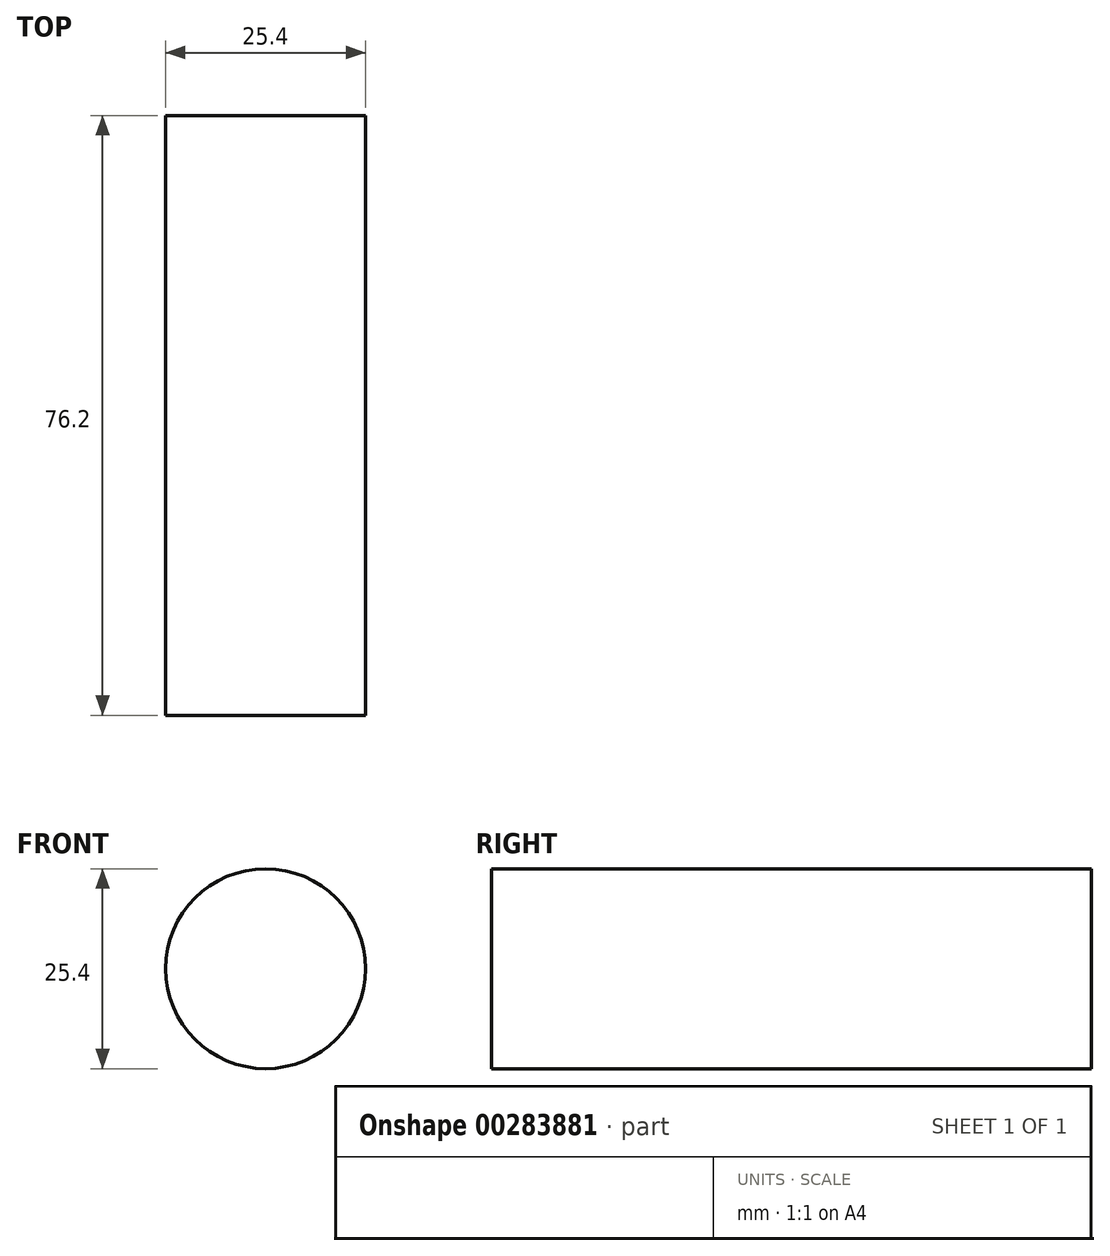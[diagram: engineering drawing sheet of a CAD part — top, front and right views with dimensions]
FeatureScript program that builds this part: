
annotation { "Feature Type Name" : "Feature", "Feature Type Description" : "" }
export const myFeature = defineFeature(function(context is Context, id is Id, definition is map)
    precondition{}
    {
        {
            var Q0;
            Q0=qCreatedBy(makeId("Front.planeOp"),FACE);
            var sketch = newSketch(context, id + "F0", { "sketchPlane" : qUnion([Q0])});
            skCircle(sketch, "E0", {"center": v(-26.7, 23.55) * mm, "radius": 12.7 * mm});
            skSolve(sketch);
        }
        {
            var Q0;
            Q0 = qSketchRegion(id + "F0", true);
            extrude(context, id + "F1", {"entities" : qUnion([Q0]), "depth" : 76.2 * mm});
        }
    });
